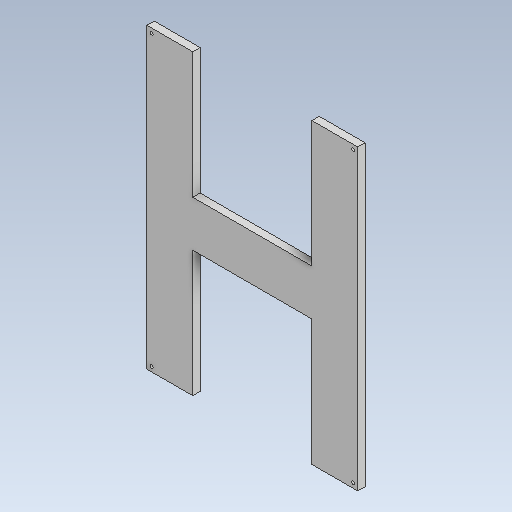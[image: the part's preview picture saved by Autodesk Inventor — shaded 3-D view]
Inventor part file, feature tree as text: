
AUTODESK INVENTOR PART (.ipt)
format: ipt  version: 2020 (Build 240168000, 168)  size: 120,320 bytes
history: native  units: mm
features: sketch x3, extrude x2, hole x1
ambient origin geometry x8: Origin, YZ Plane, XZ Plane, XY Plane, X Axis, Y Axis, Z Axis, Center Point
bodies: Solid1 (feature_tree)
feature tree (6):
  extrude  "Extrusion1"  Depth=325.0mm
  hole  "Hole1"  [1 undecoded]
  extrude  "Extrusion2"  Depth=50.0mm
  sketch  "Sketch1"  dims[d0=230.0mm d1=325.0mm]
  sketch  "Sketch2"  dims[d2=8.0mm d3=0.0mm d4=5.0mm]
  sketch  "Sketch3"  dims[d5=5.0mm d6=3.5mm d7=6.0mm d8=4.0mm d9=2.0mm d10=90.0deg d11=21.0mm d12=0.0mm d13=50.0mm d14=50.0mm d15=25.0mm d16=25.0mm d17=10.0mm d18=0.0mm]
note: 1 required parameter value undecoded (feature->parameter linkage not recoverable at this tier; creation-order binding heuristic only, values carry confidence <= 0.55)
